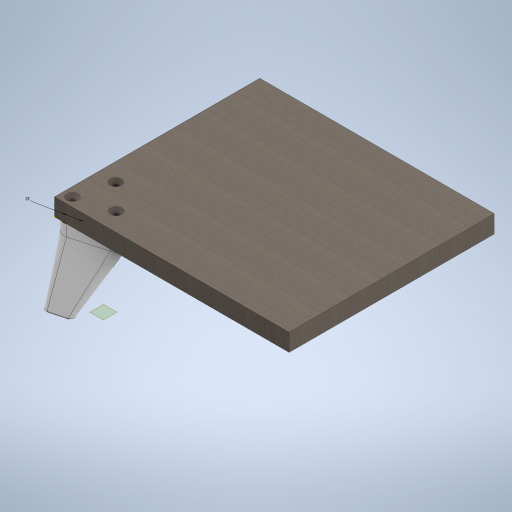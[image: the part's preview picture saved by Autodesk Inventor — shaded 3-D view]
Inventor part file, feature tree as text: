
AUTODESK INVENTOR PART (.ipt)
format: ipt  version: 2024.1 (Build 281209000, 209)  size: 532,480 bytes
history: native  units: mm
features: sketch x7, extrude x5, plane x3, chamfer x2, other x2, projected_geometry x2, loft x1
ambient origin geometry x8: Origin, YZ Plane, XZ Plane, XY Plane, X Axis, Y Axis, Z Axis, Center Point
bodies: Solid1 (feature_tree)
feature tree (22):
  extrude  "Extrusion1"  Depth=175.0mm
  extrude  "Extrusion3"  Depth=15.0mm
  chamfer  "Chamfer2"  Distance=30.0mm Angle=360.0deg
  extrude  "Extrusion4"  TaperAngle=0.0deg  [1 undecoded]
  sketch  "Sketch7"  dims[d16=7.5mm]
  plane  "Work Plane3"
  plane  "Work Plane4"
  loft  "Loft1"
  chamfer  "Chamfer4"  Distance=15.0mm
  extrude  "Extrusion5"  Depth=10.0mm TaperAngle=0.0deg
  plane  "Work Plane1"
  extrude  "Extrusion6"  Depth=2.0mm TaperAngle=45.0deg
  sketch  "Sketch1"  dims[d0=200.0mm d1=175.0mm]
  sketch  "Sketch3"  dims[d2=15.0mm d3=0.0mm d12=35.0mm]
  sketch  "Sketch4"  dims[d13=20.0mm]
  other  "leggie-boi"
  sketch  "Sketch5"  dims[d14=20.0mm]
  sketch  "Sketch6"  dims[d15=4.0mm]
  projected_geometry  "Projected Loop1"
  sketch  "Sketch9"  dims[d17=7.752551mm d18=30.0mm d20=360.0deg d22=0.0mm d23=0.0mm d24=2.8mm d25=2.0mm d26=45.0deg d27=15.0mm d31=10.0mm d32=0.0mm d36=2.5mm d37=2.0mm d38=45.0deg d39=0.0mm d40=0.0mm d46=60.0deg d47=60.0deg d48=8.0mm d49=2.8mm d50=60.0deg d51=60.0deg d52=60.0deg d53=60.0deg d54=60.25mm d55=50.5mm d56=0.0mm d62=60.0mm d65=7.0mm d66=2.7mm d67=2.7mm d68=3.0mm d69=0.0mm d70=90.0deg d71=0.0mm d72=90.0deg]
  projected_geometry  "Projected Loop2"
  other  "Edges1"
note: 1 required parameter value undecoded (feature->parameter linkage not recoverable at this tier; creation-order binding heuristic only, values carry confidence <= 0.55)
